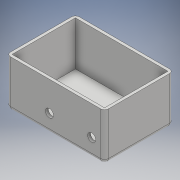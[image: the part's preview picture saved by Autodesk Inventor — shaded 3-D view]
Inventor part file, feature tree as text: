
AUTODESK INVENTOR PART (.ipt)
format: ipt  version: 2018 (Build 220112000, 112)  size: 137,216 bytes
history: native  units: mm
features: extrude x3, sketch x3, fillet x1
ambient origin geometry x8: Origin, YZ Plane, XZ Plane, XY Plane, X Axis, Y Axis, Z Axis, Center Point
bodies: Solid1 (feature_tree)
feature tree (7):
  extrude  "Extrusion1"  Depth=31.5mm
  extrude  "Extrusion2"  Depth=22.0mm TaperAngle=0.0deg
  extrude  "Extrusion3"  Depth=2.0mm
  fillet  "Fillet1"  Radius=20.0mm
  sketch  "Sketch1"  dims[d0=46.0mm d1=31.5mm]
  sketch  "Sketch2"  dims[d2=1.4mm d3=22.0mm d4=0.0mm]
  sketch  "Sketch3"  dims[d5=1.4mm d6=0.0mm d7=4.0mm d8=20.0mm d9=4.0mm d10=5.0mm d11=1.4mm d12=0.0mm d13=2.0mm]
